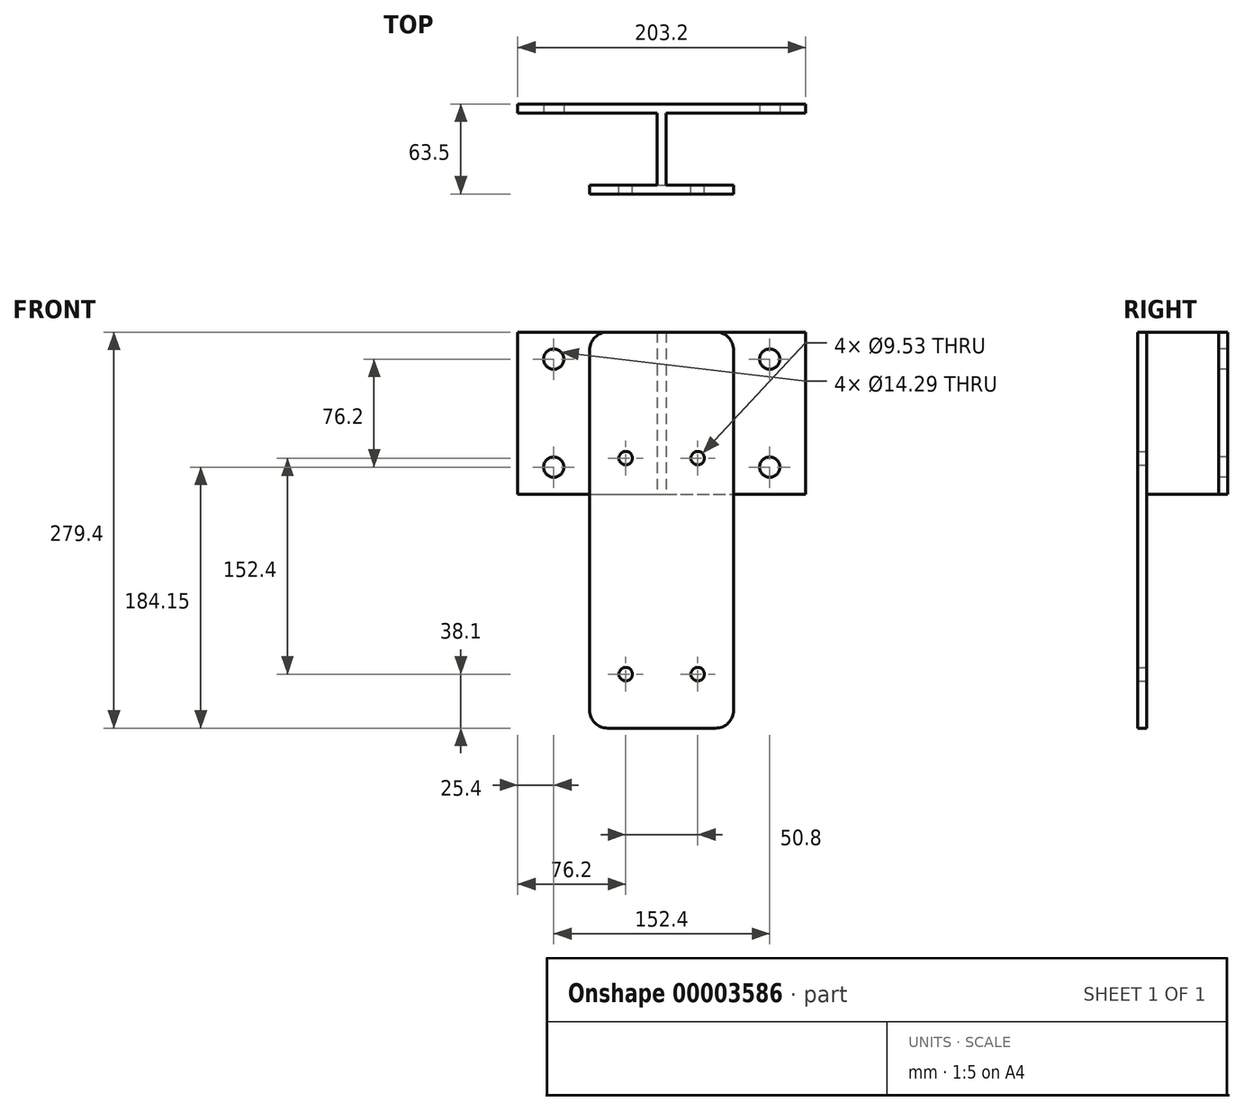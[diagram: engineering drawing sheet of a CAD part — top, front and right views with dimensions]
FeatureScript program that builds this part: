
annotation { "Feature Type Name" : "Feature", "Feature Type Description" : "" }
export const myFeature = defineFeature(function(context is Context, id is Id, definition is map)
    precondition{}
    {
        {
            var Q0;
            Q0=qCreatedBy(makeId("Front.planeOp"),FACE);
            var sketch = newSketch(context, id + "F0", { "sketchPlane" : qUnion([Q0])});
            skLineSegment(sketch, "E0.rect.bottom", {"start": v(-50.8, 139.7) * mm, "end": v(50.8, 139.7) * mm});
            skLineSegment(sketch, "E0.rect.top", {"start": v(-50.8, -139.7) * mm, "end": v(50.8, -139.7) * mm});
            skLineSegment(sketch, "E0.rect.left", {"start": v(-50.8, 139.7) * mm, "end": v(-50.8, -139.7) * mm});
            skLineSegment(sketch, "E0.rect.right", {"start": v(50.8, 139.7) * mm, "end": v(50.8, -139.7) * mm});
            skPoint(sketch, "E0.rect.middle", {"position": v(0, 0) * mm});
            skLineSegment(sketch, "E1.0", {"start": v(-50.8, -101.6) * mm, "end": v(50.8, -101.6) * mm, "construction": true});
            skLineSegment(sketch, "E2.0", {"start": v(-50.8, 50.8) * mm, "end": v(50.8, 50.8) * mm, "construction": true});
            skLineSegment(sketch, "E3", {"start": v(0, 139.7) * mm, "end": v(0, -139.7) * mm, "construction": true});
            skLineSegment(sketch, "E4.0", {"start": v(-25.4, 139.7) * mm, "end": v(-25.4, -139.7) * mm, "construction": true});
            skCircle(sketch, "E5", {"center": v(-25.4, 50.8) * mm, "radius": 4.76 * mm});
            skCircle(sketch, "E6", {"center": v(-25.4, -101.6) * mm, "radius": 4.76 * mm});
            skCircle(sketch, "E7.0.MirrorC", {"center": v(25.4, 50.8) * mm, "radius": 4.76 * mm});
            skCircle(sketch, "E8.0.MirrorC", {"center": v(25.4, -101.6) * mm, "radius": 4.76 * mm});
            skSolve(sketch);
        }
        {
            var Q0;
            Q0 = qSketchRegion(id + "F0", true);
            extrude(context, id + "F1", {"entities" : qUnion([Q0]), "depth" : 6.35 * mm});
        }
        {
            var Q0;
            Q0=makeQuery(id+"F1.opExtrude","SWEPT_EDGE",EDGE,{"disambiguationData":[OSD([sQuery(id+"F0.wireOp",EDGE,"E0.rect.bottom"),sQuery(id+"F0.wireOp",EDGE,"E0.rect.right")])]});
            var Q1;
            Q1=makeQuery(id+"F1.opExtrude","SWEPT_EDGE",EDGE,{"disambiguationData":[OSD([sQuery(id+"F0.wireOp",EDGE,"E0.rect.bottom"),sQuery(id+"F0.wireOp",EDGE,"E0.rect.left")])]});
            fillet(context, id + "F2", {"entities" : qUnion([Q0, Q1]), "radius" : 12.7 * mm, "tangentPropagation" : true, "allowEdgeOverflow" : false});
        }
        {
            var Q0;
            Q0=makeQuery(id+"F1.opExtrude","SWEPT_EDGE",EDGE,{"disambiguationData":[OSD([sQuery(id+"F0.wireOp",EDGE,"E0.rect.top"),sQuery(id+"F0.wireOp",EDGE,"E0.rect.right")])]});
            var Q1;
            Q1=makeQuery(id+"F1.opExtrude","SWEPT_EDGE",EDGE,{"disambiguationData":[OSD([sQuery(id+"F0.wireOp",EDGE,"E0.rect.top"),sQuery(id+"F0.wireOp",EDGE,"E0.rect.left")])]});
            fillet(context, id + "F3", {"entities" : qUnion([Q0, Q1]), "radius" : 12.7 * mm, "tangentPropagation" : true, "allowEdgeOverflow" : false});
        }
        {
            var Q0;
            Q0=makeQuery(id+"F1.opExtrude","CAP_FACE",FACE,{"disambiguationData":[OSD([sQuery(id+"F0.wireOp",EDGE,"E0.rect.bottom"),sQuery(id+"F0.wireOp",EDGE,"E0.rect.top"),sQuery(id+"F0.wireOp",EDGE,"E0.rect.left"),sQuery(id+"F0.wireOp",EDGE,"E0.rect.right"),sQuery(id+"F0.wireOp",EDGE,"E5"),sQuery(id+"F0.wireOp",EDGE,"E6"),sQuery(id+"F0.wireOp",EDGE,"E7.0.MirrorC"),sQuery(id+"F0.wireOp",EDGE,"E8.0.MirrorC")])],"isStart":true});
            var sketch = newSketch(context, id + "F4", { "sketchPlane" : qUnion([Q0])});
            skLineSegment(sketch, "E9", {"start": v(0, 139.7) * mm, "end": v(0, -127.87) * mm, "construction": true});
            skLineSegment(sketch, "E10.0", {"start": v(-3.18, 139.7) * mm, "end": v(-3.18, 25.4) * mm});
            skLineSegment(sketch, "E11.0", {"start": v(3.17, 139.7) * mm, "end": v(3.17, 25.4) * mm});
            skLineSegment(sketch, "E12.0", {"start": v(3.17, 25.4) * mm, "end": v(-3.18, 25.4) * mm});
            skLineSegment(sketch, "E13.0", {"start": v(3.17, 139.7) * mm, "end": v(-3.18, 139.7) * mm});
            skPoint(sketch, "E14.orphan", {"position": v(-38.1, 139.7) * mm});
            skPoint(sketch, "E15.orphan", {"position": v(38.1, 139.7) * mm});
            skSolve(sketch);
        }
        {
            var Q0;
            Q0 = qSketchRegion(id + "F4", true);
            extrude(context, id + "F5", {"entities" : qUnion([Q0]), "operationType" : NewBodyOperationType.ADD, "depth" : 50.8 * mm});
        }
        {
            var Q0;
            Q0=makeQuery(id+"F5.opExtrude","CAP_FACE",FACE,{"disambiguationData":[OSD([sQuery(id+"F4.wireOp",EDGE,"E10.0"),sQuery(id+"F4.wireOp",EDGE,"E11.0"),sQuery(id+"F4.wireOp",EDGE,"E12.0"),sQuery(id+"F4.wireOp",EDGE,"E13.0")])],"isStart":false});
            var sketch = newSketch(context, id + "F6", { "sketchPlane" : qUnion([Q0])});
            skLineSegment(sketch, "E16", {"start": v(0, 139.7) * mm, "end": v(0, 25.4) * mm, "construction": true});
            skLineSegment(sketch, "E17.0", {"start": v(-101.6, 139.7) * mm, "end": v(-101.6, 25.4) * mm});
            skLineSegment(sketch, "E18.0.MirrorCS", {"start": v(101.6, 139.7) * mm, "end": v(101.6, 25.4) * mm});
            skLineSegment(sketch, "E19", {"start": v(-101.6, 25.4) * mm, "end": v(101.6, 25.4) * mm});
            skLineSegment(sketch, "E20", {"start": v(101.6, 139.7) * mm, "end": v(-101.6, 139.7) * mm});
            skLineSegment(sketch, "E21", {"start": v(-101.6, 82.55) * mm, "end": v(101.6, 82.55) * mm, "construction": true});
            skLineSegment(sketch, "E22.0", {"start": v(-76.2, 139.7) * mm, "end": v(-76.2, 25.4) * mm, "construction": true});
            skLineSegment(sketch, "E23.0", {"start": v(76.2, 139.7) * mm, "end": v(76.2, 25.4) * mm, "construction": true});
            skLineSegment(sketch, "E24.0", {"start": v(-101.6, 44.45) * mm, "end": v(101.6, 44.45) * mm, "construction": true});
            skCircle(sketch, "E25", {"center": v(-76.2, 44.45) * mm, "radius": 7.14 * mm});
            skCircle(sketch, "E26", {"center": v(76.2, 44.45) * mm, "radius": 7.14 * mm});
            skCircle(sketch, "E27.0.MirrorC", {"center": v(-76.2, 120.65) * mm, "radius": 7.14 * mm});
            skCircle(sketch, "E28.0.MirrorC", {"center": v(76.2, 120.65) * mm, "radius": 7.14 * mm});
            skSolve(sketch);
        }
        {
            var Q0;
            Q0 = qSketchRegion(id + "F6", true);
            extrude(context, id + "F7", {"entities" : qUnion([Q0]), "operationType" : NewBodyOperationType.ADD, "depth" : 6.35 * mm});
        }
    });
